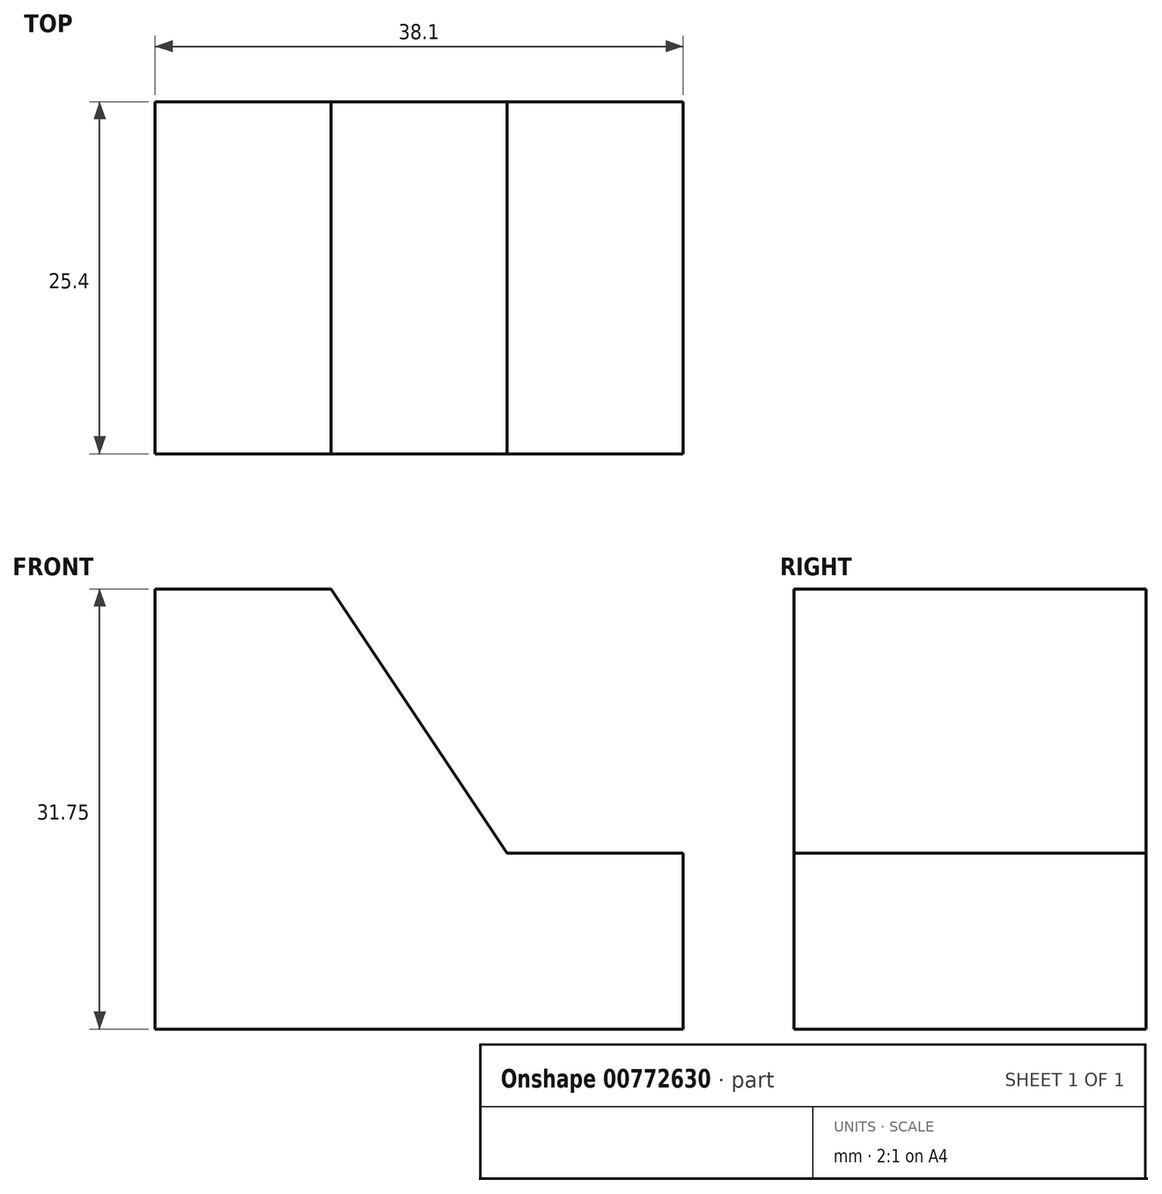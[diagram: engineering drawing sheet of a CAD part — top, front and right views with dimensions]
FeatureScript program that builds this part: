
annotation { "Feature Type Name" : "Feature", "Feature Type Description" : "" }
export const myFeature = defineFeature(function(context is Context, id is Id, definition is map)
    precondition{}
    {
        {
            var Q0;
            Q0=qCreatedBy(makeId("Front.planeOp"),FACE);
            var sketch = newSketch(context, id + "F0", { "sketchPlane" : qUnion([Q0])});
            skLineSegment(sketch, "E0", {"start": v(0, 0) * mm, "end": v(0, 31.75) * mm});
            skLineSegment(sketch, "E1", {"start": v(0, 0) * mm, "end": v(38.1, 0) * mm});
            skLineSegment(sketch, "E2", {"start": v(38.1, 0) * mm, "end": v(38.1, 12.7) * mm});
            skLineSegment(sketch, "E3", {"start": v(38.1, 12.7) * mm, "end": v(25.4, 12.7) * mm});
            skLineSegment(sketch, "E4", {"start": v(0, 31.75) * mm, "end": v(12.7, 31.75) * mm});
            skLineSegment(sketch, "E5", {"start": v(12.7, 31.75) * mm, "end": v(25.4, 12.7) * mm});
            skSolve(sketch);
        }
        {
            var Q0;
            Q0 = qSketchRegion(id + "F0", true);
            extrude(context, id + "F1", {"entities" : qUnion([Q0]), "depth" : 25.4 * mm, "offsetDistance" : 25.4 * mm});
        }
    });
